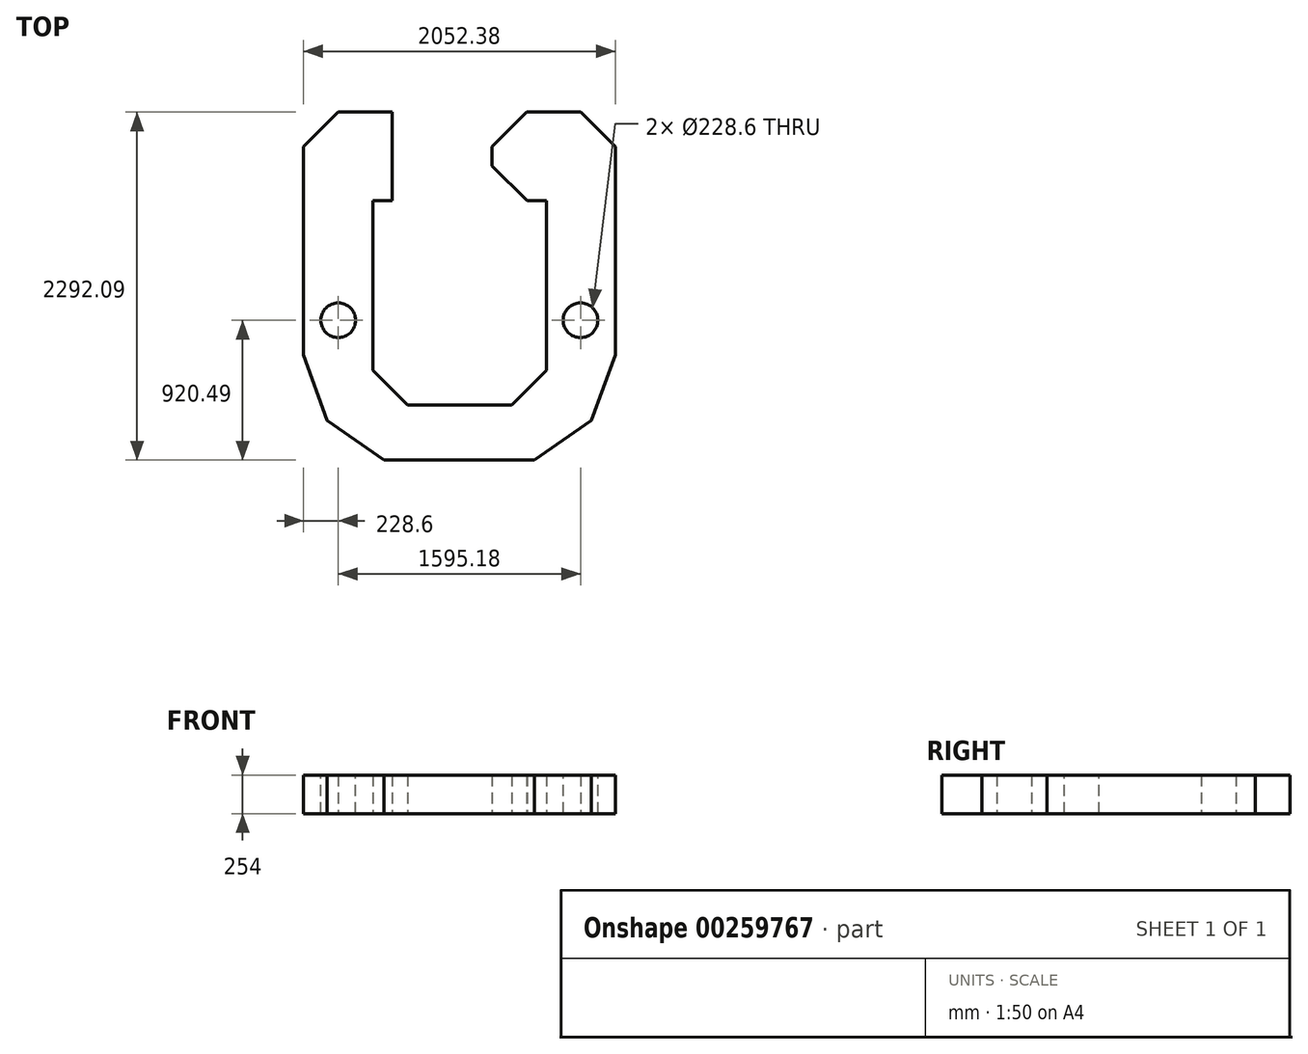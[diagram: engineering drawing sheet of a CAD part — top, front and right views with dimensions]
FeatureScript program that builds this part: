
annotation { "Feature Type Name" : "Feature", "Feature Type Description" : "" }
export const myFeature = defineFeature(function(context is Context, id is Id, definition is map)
    precondition{}
    {
        {
            var Q0;
            Q0=qCreatedBy(makeId("Top.planeOp"),FACE);
            var sketch = newSketch(context, id + "F0", { "sketchPlane" : qUnion([Q0])});
            skLineSegment(sketch, "E0", {"start": v(0, 0) * mm, "end": v(-355.6, 0) * mm});
            skLineSegment(sketch, "E1", {"start": v(-584.2, -228.6) * mm, "end": v(-355.6, 0) * mm});
            skLineSegment(sketch, "E2", {"start": v(-584.2, -228.6) * mm, "end": v(-584.2, -1371.6) * mm});
            skLineSegment(sketch, "E3", {"start": v(0, 0) * mm, "end": v(0, -584.2) * mm});
            skLineSegment(sketch, "E4", {"start": v(0, -584.2) * mm, "end": v(-127, -584.2) * mm});
            skLineSegment(sketch, "E5", {"start": v(-127, -584.2) * mm, "end": v(-127, -1701.8) * mm});
            skLineSegment(sketch, "E6", {"start": v(101.6, -1930.4) * mm, "end": v(-127, -1701.8) * mm});
            skLineSegment(sketch, "E7", {"start": v(101.6, -1930.4) * mm, "end": v(787.4, -1930.4) * mm});
            skLineSegment(sketch, "E8", {"start": v(444.5, -1930.4) * mm, "end": v(444.5, -1889.02) * mm});
            skLineSegment(sketch, "E9.MirrorCS", {"start": v(787.4, -1930.4) * mm, "end": v(1016, -1701.8) * mm});
            skLineSegment(sketch, "E10", {"start": v(1016, -1701.8) * mm, "end": v(1016, -584.2) * mm});
            skLineSegment(sketch, "E11", {"start": v(1016, -584.2) * mm, "end": v(889, -584.2) * mm});
            skLineSegment(sketch, "E12", {"start": v(655.38, -355.63) * mm, "end": v(889, -584.2) * mm});
            skLineSegment(sketch, "E13", {"start": v(655.38, -355.63) * mm, "end": v(655.38, -228.63) * mm});
            skLineSegment(sketch, "E14", {"start": v(883.98, 0) * mm, "end": v(655.38, -228.63) * mm});
            skLineSegment(sketch, "E15", {"start": v(883.98, 0) * mm, "end": v(1239.58, 0) * mm});
            skLineSegment(sketch, "E16", {"start": v(1468.18, -228.63) * mm, "end": v(1239.58, 0) * mm});
            skLineSegment(sketch, "E17", {"start": v(1468.18, -228.63) * mm, "end": v(1468.18, -1600.23) * mm});
            skLineSegment(sketch, "E18", {"start": v(1468.18, -1600.23) * mm, "end": v(1311.8, -2029.85) * mm});
            skLineSegment(sketch, "E19", {"start": v(1311.8, -2029.85) * mm, "end": v(937.29, -2292.1) * mm});
            skLineSegment(sketch, "E20", {"start": v(937.29, -2292.1) * mm, "end": v(607.09, -2292.1) * mm});
            skLineSegment(sketch, "E21", {"start": v(607.09, -2292.1) * mm, "end": v(276.89, -2292.1) * mm});
            skLineSegment(sketch, "E22", {"start": v(276.89, -2292.1) * mm, "end": v(276.89, -1930.4) * mm});
            skLineSegment(sketch, "E23", {"start": v(607.09, -2292.1) * mm, "end": v(607.09, -1930.4) * mm});
            skLineSegment(sketch, "E24", {"start": v(276.89, -2292.1) * mm, "end": v(-53.31, -2292.1) * mm});
            skLineSegment(sketch, "E25", {"start": v(-53.31, -2292.1) * mm, "end": v(-427.83, -2029.85) * mm});
            skLineSegment(sketch, "E26", {"start": v(-427.83, -2029.85) * mm, "end": v(-584.2, -1600.23) * mm});
            skLineSegment(sketch, "E27", {"start": v(-584.2, -1371.6) * mm, "end": v(-584.2, -1858.55) * mm});
            skSolve(sketch);
        }
        {
            var Q0;
            Q0=makeQuery(id+"F0.imprint","IMPRINT",FACE,{"disambiguationData":[TD([[makeQuery(id+"F0.imprint","IMPRINT",EDGE,{"derivedFrom":sQuery(id+"F0.wireOp",EDGE,"E0")}),1.0]])]});
            var Q1;
            Q1=makeQuery(id+"F0.imprint","IMPRINT",FACE,{"disambiguationData":[TD([[makeQuery(id+"F0.imprint","IMPRINT",EDGE,{"derivedFrom":sQuery(id+"F0.wireOp",EDGE,"E21")}),-1.0]])]});
            var Q2;
            {var subQ0=sQuery(id+"F0.wireOp",EDGE,"E9.MirrorCS");Q2=makeQuery(id+"F0.imprint","IMPRINT",FACE,{"disambiguationData":[TD([[makeQuery(id+"F0.imprint","IMPRINT",EDGE,{"derivedFrom":subQ0}),-1.0]])]});}
            extrude(context, id + "F1", {"entities" : qUnion([Q0, Q1, Q2]), "depth" : 254 * mm});
        }
        {
            var Q0;
            Q0=makeQuery(id+"F1.opExtrude","CAP_FACE",FACE,{"disambiguationData":[OSD([sQuery(id+"F0.wireOp",EDGE,"E0"),sQuery(id+"F0.wireOp",EDGE,"E1"),sQuery(id+"F0.wireOp",EDGE,"E2"),sQuery(id+"F0.wireOp",EDGE,"E3"),sQuery(id+"F0.wireOp",EDGE,"E4"),sQuery(id+"F0.wireOp",EDGE,"E5"),sQuery(id+"F0.wireOp",EDGE,"E6"),sQuery(id+"F0.wireOp",EDGE,"E7"),sQuery(id+"F0.wireOp",EDGE,"E9.MirrorCS"),sQuery(id+"F0.wireOp",EDGE,"E10"),sQuery(id+"F0.wireOp",EDGE,"E11"),sQuery(id+"F0.wireOp",EDGE,"E12"),sQuery(id+"F0.wireOp",EDGE,"E13"),sQuery(id+"F0.wireOp",EDGE,"E14"),sQuery(id+"F0.wireOp",EDGE,"E15"),sQuery(id+"F0.wireOp",EDGE,"E16"),sQuery(id+"F0.wireOp",EDGE,"E17"),sQuery(id+"F0.wireOp",EDGE,"E18"),sQuery(id+"F0.wireOp",EDGE,"E19"),sQuery(id+"F0.wireOp",EDGE,"E20"),sQuery(id+"F0.wireOp",EDGE,"E21"),sQuery(id+"F0.wireOp",EDGE,"E24"),sQuery(id+"F0.wireOp",EDGE,"E25"),sQuery(id+"F0.wireOp",EDGE,"E26"),sQuery(id+"F0.wireOp",EDGE,"E27")])],"isStart":false});
            var sketch = newSketch(context, id + "F2", { "sketchPlane" : qUnion([Q0])});
            skLineSegment(sketch, "E28.0.0", {"start": v(-584.2, -228.6) * mm, "end": v(-584.2, -1600.23) * mm});
            skLineSegment(sketch, "E28.0.1", {"start": v(-584.2, -1600.23) * mm, "end": v(-427.83, -2029.85) * mm});
            skLineSegment(sketch, "E28.0.2", {"start": v(-427.83, -2029.85) * mm, "end": v(-53.31, -2292.1) * mm});
            skLineSegment(sketch, "E28.0.3", {"start": v(-53.31, -2292.1) * mm, "end": v(937.29, -2292.1) * mm});
            skLineSegment(sketch, "E28.0.4", {"start": v(937.29, -2292.1) * mm, "end": v(1311.8, -2029.85) * mm});
            skLineSegment(sketch, "E28.0.5", {"start": v(1311.8, -2029.85) * mm, "end": v(1468.18, -1600.23) * mm});
            skLineSegment(sketch, "E28.0.6", {"start": v(1468.18, -1600.23) * mm, "end": v(1468.18, -228.63) * mm});
            skLineSegment(sketch, "E28.0.7", {"start": v(1468.18, -228.63) * mm, "end": v(1239.58, 0) * mm});
            skLineSegment(sketch, "E28.0.8", {"start": v(1239.58, 0) * mm, "end": v(883.98, 0) * mm});
            skLineSegment(sketch, "E28.0.9", {"start": v(883.98, 0) * mm, "end": v(655.38, -228.63) * mm});
            skLineSegment(sketch, "E28.0.10", {"start": v(655.38, -228.63) * mm, "end": v(655.38, -355.63) * mm});
            skLineSegment(sketch, "E28.0.11", {"start": v(655.38, -355.63) * mm, "end": v(889, -584.2) * mm});
            skLineSegment(sketch, "E28.0.12", {"start": v(889, -584.2) * mm, "end": v(1016, -584.2) * mm});
            skLineSegment(sketch, "E28.0.13", {"start": v(1016, -584.2) * mm, "end": v(1016, -1701.8) * mm});
            skLineSegment(sketch, "E28.0.14", {"start": v(1016, -1701.8) * mm, "end": v(787.4, -1930.4) * mm});
            skLineSegment(sketch, "E28.0.15", {"start": v(787.4, -1930.4) * mm, "end": v(101.6, -1930.4) * mm});
            skLineSegment(sketch, "E28.0.16", {"start": v(101.6, -1930.4) * mm, "end": v(-127, -1701.8) * mm});
            skLineSegment(sketch, "E28.0.17", {"start": v(-127, -1701.8) * mm, "end": v(-127, -584.2) * mm});
            skLineSegment(sketch, "E28.0.18", {"start": v(-127, -584.2) * mm, "end": v(0, -584.2) * mm});
            skLineSegment(sketch, "E28.0.19", {"start": v(0, -584.2) * mm, "end": v(0, 0) * mm});
            skLineSegment(sketch, "E28.0.20", {"start": v(0, 0) * mm, "end": v(-355.6, 0) * mm});
            skLineSegment(sketch, "E28.0.21", {"start": v(-355.6, 0) * mm, "end": v(-584.2, -228.6) * mm});
            skCircle(sketch, "E29", {"center": v(-355.6, -1371.6) * mm, "radius": 114.3 * mm});
            skCircle(sketch, "E30", {"center": v(1239.58, -1371.6) * mm, "radius": 114.3 * mm});
            skSolve(sketch);
        }
        {
            var Q0;
            Q0=makeQuery(id+"F2.imprint","IMPRINT",FACE,{"disambiguationData":[TD([[makeQuery(id+"F2.imprint","IMPRINT",EDGE,{"derivedFrom":sQuery(id+"F2.wireOp",EDGE,"E29")}),1.0]])]});
            var Q1;
            Q1=makeQuery(id+"F2.imprint","IMPRINT",FACE,{"disambiguationData":[TD([[makeQuery(id+"F2.imprint","IMPRINT",EDGE,{"derivedFrom":sQuery(id+"F2.wireOp",EDGE,"E30")}),1.0]])]});
            extrude(context, id + "F3", {"entities" : qUnion([Q0, Q1]), "operationType" : NewBodyOperationType.REMOVE, "oppositeDirection" : true, "depth" : 508 * mm});
        }
    });
